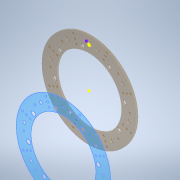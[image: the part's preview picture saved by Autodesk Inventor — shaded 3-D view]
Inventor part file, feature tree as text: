
AUTODESK INVENTOR PART (.ipt)
format: ipt  version: 2020 (Build 240168000, 168)  size: 268,800 bytes
history: native  units: in
note: dims shown in document units (in); Inventor stores cm internally (conversion verified against a paired STEP export)
features: extrude x2, sketch x2
ambient origin geometry x8: Origin, YZ Plane, XZ Plane, XY Plane, X Axis, Y Axis, Z Axis, Center Point
bodies: Solid1 (feature_tree)
feature tree (4):
  extrude  "Extrusion1"  Depth=1.75in
  extrude  "Extrusion2"  Depth=0.25in
  sketch  "Sketch1"  dims[d0=7.75in d1=1.75in]
  sketch  "Sketch2"  dims[d2=0.25in d3=0.0in d4=0.2031in d5=4.735in d6=0.0773in d7=22.5deg d8=0.2319in d9=0.35in d10=3.1496in d12=360.0deg d14=5.25in d15=1.1811in d17=0.5in d18=0.3937in d20=1.0in d22=4.5in d34=0.25in d35=0.0in d36=0.5in d37=4.25in d38=0.2319in d39=3.1496in d41=360.0deg d43=3.1496in d45=360.0deg d47=5.25in d48=3.1496in d50=360.0deg]
